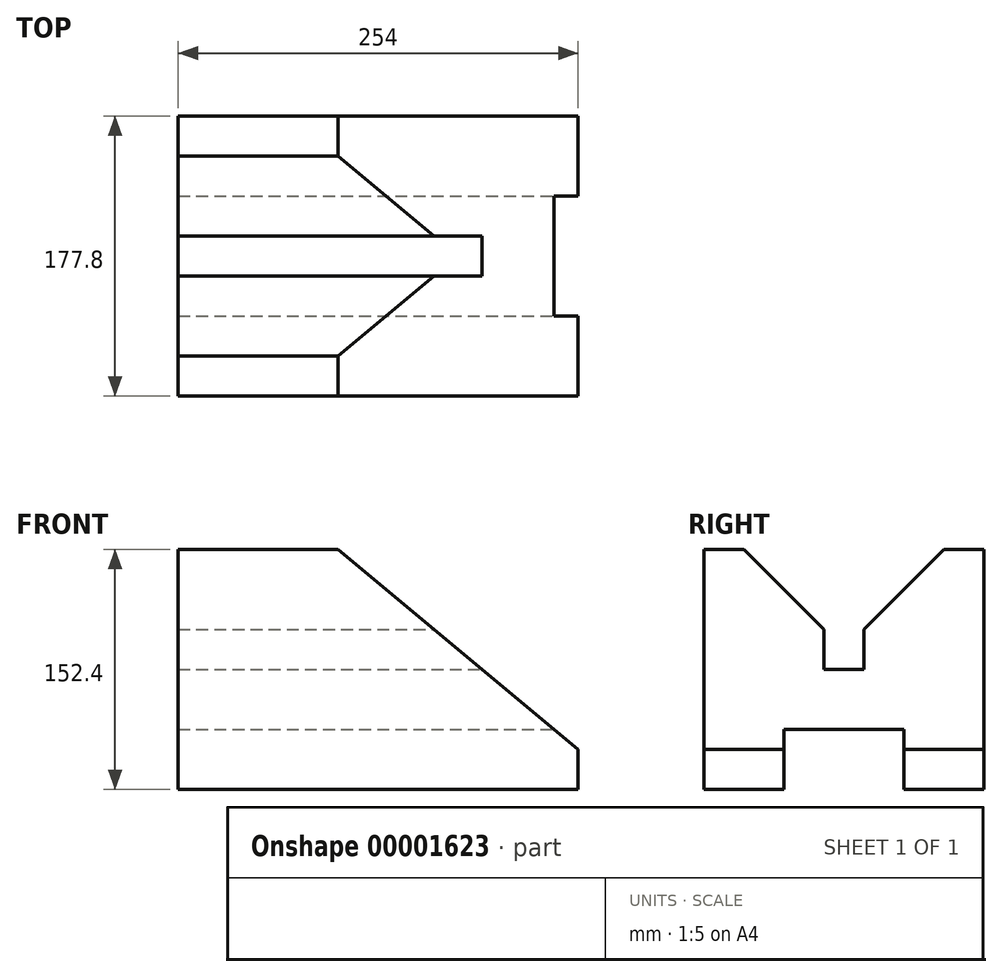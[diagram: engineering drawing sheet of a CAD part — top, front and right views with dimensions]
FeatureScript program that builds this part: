
annotation { "Feature Type Name" : "Feature", "Feature Type Description" : "" }
export const myFeature = defineFeature(function(context is Context, id is Id, definition is map)
    precondition{}
    {
        {
            var Q0;
            Q0=qCreatedBy(makeId("Top.planeOp"),FACE);
            var sketch = newSketch(context, id + "F0", { "sketchPlane" : qUnion([Q0])});
            skLineSegment(sketch, "E0.bottom", {"start": v(0, 0) * mm, "end": v(254, 0) * mm});
            skLineSegment(sketch, "E0.top", {"start": v(0, 177.8) * mm, "end": v(254, 177.8) * mm});
            skLineSegment(sketch, "E0.left", {"start": v(0, 0) * mm, "end": v(0, 177.8) * mm});
            skLineSegment(sketch, "E0.right", {"start": v(254, 0) * mm, "end": v(254, 177.8) * mm});
            skSolve(sketch);
        }
        {
            var Q0;
            Q0 = qSketchRegion(id + "F0", true);
            extrude(context, id + "F1", {"entities" : qUnion([Q0]), "depth" : 152.4 * mm});
        }
        {
            var Q0;
            Q0=makeQuery(id+"F1.opExtrude","SWEPT_FACE",FACE,{"disambiguationData":[OSD([sQuery(id+"F0.wireOp",EDGE,"E0.bottom")])]});
            var sketch = newSketch(context, id + "F2", { "sketchPlane" : qUnion([Q0])});
            skLineSegment(sketch, "E1", {"start": v(254, 152.4) * mm, "end": v(101.6, 152.4) * mm});
            skLineSegment(sketch, "E2", {"start": v(101.6, 152.4) * mm, "end": v(254, 25.4) * mm});
            skLineSegment(sketch, "E3", {"start": v(254, 25.4) * mm, "end": v(254, 152.4) * mm});
            skSolve(sketch);
        }
        {
            var Q0;
            Q0 = qSketchRegion(id + "F2", true);
            extrude(context, id + "F3", {"entities" : qUnion([Q0]), "operationType" : NewBodyOperationType.REMOVE, "endBound" : BoundingType.THROUGH_ALL, "oppositeDirection" : true, "depth" : 25.4 * mm});
        }
        {
            var Q0;
            Q0=makeQuery(id+"F1.opExtrude","SWEPT_FACE",FACE,{"disambiguationData":[OSD([sQuery(id+"F0.wireOp",EDGE,"E0.right")])]});
            var sketch = newSketch(context, id + "F4", { "sketchPlane" : qUnion([Q0])});
            skLineSegment(sketch, "E4.bottom", {"start": v(50.8, 0) * mm, "end": v(127, 0) * mm});
            skLineSegment(sketch, "E4.top", {"start": v(50.8, 38.1) * mm, "end": v(127, 38.1) * mm});
            skLineSegment(sketch, "E4.left", {"start": v(50.8, 0) * mm, "end": v(50.8, 38.1) * mm});
            skLineSegment(sketch, "E4.right", {"start": v(127, 0) * mm, "end": v(127, 38.1) * mm});
            skLineSegment(sketch, "E5", {"start": v(25.4, 152.4) * mm, "end": v(76.2, 101.6) * mm});
            skLineSegment(sketch, "E6", {"start": v(76.2, 101.6) * mm, "end": v(76.2, 76.2) * mm});
            skLineSegment(sketch, "E7", {"start": v(76.2, 76.2) * mm, "end": v(101.6, 76.2) * mm});
            skLineSegment(sketch, "E8", {"start": v(101.6, 76.2) * mm, "end": v(101.6, 101.6) * mm});
            skLineSegment(sketch, "E9", {"start": v(101.6, 101.6) * mm, "end": v(152.4, 152.4) * mm});
            skLineSegment(sketch, "E10", {"start": v(152.4, 152.4) * mm, "end": v(25.4, 152.4) * mm});
            skSolve(sketch);
        }
        {
            var Q0;
            Q0 = qSketchRegion(id + "F4", true);
            extrude(context, id + "F5", {"entities" : qUnion([Q0]), "operationType" : NewBodyOperationType.REMOVE, "endBound" : BoundingType.THROUGH_ALL, "oppositeDirection" : true, "depth" : 25.4 * mm});
        }
    });
